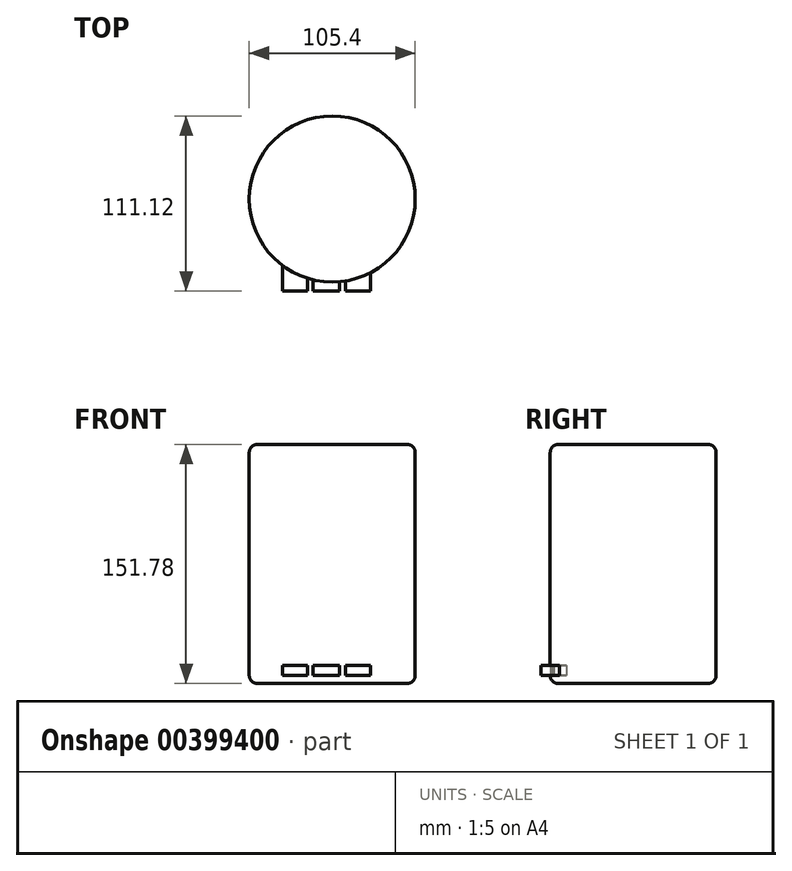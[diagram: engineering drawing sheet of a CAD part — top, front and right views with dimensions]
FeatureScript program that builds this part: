
annotation { "Feature Type Name" : "Feature", "Feature Type Description" : "" }
export const myFeature = defineFeature(function(context is Context, id is Id, definition is map)
    precondition{}
    {
        {
            var Q0;
            Q0=qCreatedBy(makeId("Front.planeOp"),FACE);
            var sketch = newSketch(context, id + "F0", { "sketchPlane" : qUnion([Q0])});
            skLineSegment(sketch, "E0.bottom", {"start": v(-52.7, -75.99) * mm, "end": v(0, -75.99) * mm});
            skLineSegment(sketch, "E0.top", {"start": v(-52.7, 75.8) * mm, "end": v(0, 75.8) * mm});
            skLineSegment(sketch, "E0.left", {"start": v(-52.7, -75.99) * mm, "end": v(-52.7, 75.8) * mm});
            skLineSegment(sketch, "E0.right", {"start": v(0, -75.99) * mm, "end": v(0, 75.8) * mm});
            skSolve(sketch);
        }
        {
            var Q0;
            Q0=makeQuery(id+"F0.imprint","IMPRINT",FACE,{"disambiguationData":[TD([[makeQuery(id+"F0.imprint","IMPRINT",EDGE,{"derivedFrom":sQuery(id+"F0.wireOp",EDGE,"E0.bottom")}),1.0]])]});
            var Q1;
            Q1=sQuery(id+"F0.wireOp",EDGE,"E0.left");
            revolve(context, id + "F1", {"entities" : qUnion([Q0]), "axis" : qUnion([Q1]), "revolveType" : RevolveType.FULL});
        }
        {
            var Q0;
            Q0=makeQuery(id+"F1.opRevolve","SWEPT_FACE",FACE,{"disambiguationData":[OSD([sQuery(id+"F0.wireOp",EDGE,"E0.top")])]});
            var Q1;
            Q1=makeQuery(id+"F1.opRevolve","SWEPT_FACE",FACE,{"disambiguationData":[OSD([sQuery(id+"F0.wireOp",EDGE,"E0.bottom")])]});
            fillet(context, id + "F2", {"entities" : qUnion([Q0, Q1]), "radius" : 5.08 * mm, "tangentPropagation" : true, "allowEdgeOverflow" : false});
        }
        {
            var Q0;
            Q0=qCreatedBy(makeId("Front.planeOp"),FACE);
            var sketch = newSketch(context, id + "F3", { "sketchPlane" : qUnion([Q0])});
            skLineSegment(sketch, "E1.bottom", {"start": v(-84.17, -70.81) * mm, "end": v(-68.26, -70.81) * mm});
            skLineSegment(sketch, "E1.top", {"start": v(-84.17, -64.49) * mm, "end": v(-68.26, -64.49) * mm});
            skLineSegment(sketch, "E1.left", {"start": v(-84.17, -70.81) * mm, "end": v(-84.17, -64.49) * mm});
            skLineSegment(sketch, "E1.right", {"start": v(-68.26, -70.81) * mm, "end": v(-68.26, -64.49) * mm});
            skLineSegment(sketch, "E2.bottom", {"start": v(-64.81, -64.49) * mm, "end": v(-48.14, -64.49) * mm});
            skLineSegment(sketch, "E2.top", {"start": v(-64.81, -71) * mm, "end": v(-48.14, -71) * mm});
            skLineSegment(sketch, "E2.left", {"start": v(-64.81, -64.49) * mm, "end": v(-64.81, -71) * mm});
            skLineSegment(sketch, "E2.right", {"start": v(-48.14, -64.49) * mm, "end": v(-48.14, -71) * mm});
            skLineSegment(sketch, "E3.bottom", {"start": v(-44.3, -64.49) * mm, "end": v(-28.4, -64.49) * mm});
            skLineSegment(sketch, "E3.top", {"start": v(-44.3, -71) * mm, "end": v(-28.4, -71) * mm});
            skLineSegment(sketch, "E3.left", {"start": v(-44.3, -64.49) * mm, "end": v(-44.3, -71) * mm});
            skLineSegment(sketch, "E3.right", {"start": v(-28.4, -64.49) * mm, "end": v(-28.4, -71) * mm});
            skSolve(sketch);
        }
        {
            var Q0;
            Q0 = qSketchRegion(id + "F3", true);
            extrude(context, id + "F4", {"entities" : qUnion([Q0]), "operationType" : NewBodyOperationType.ADD, "depth" : 58.42 * mm});
        }
    });
